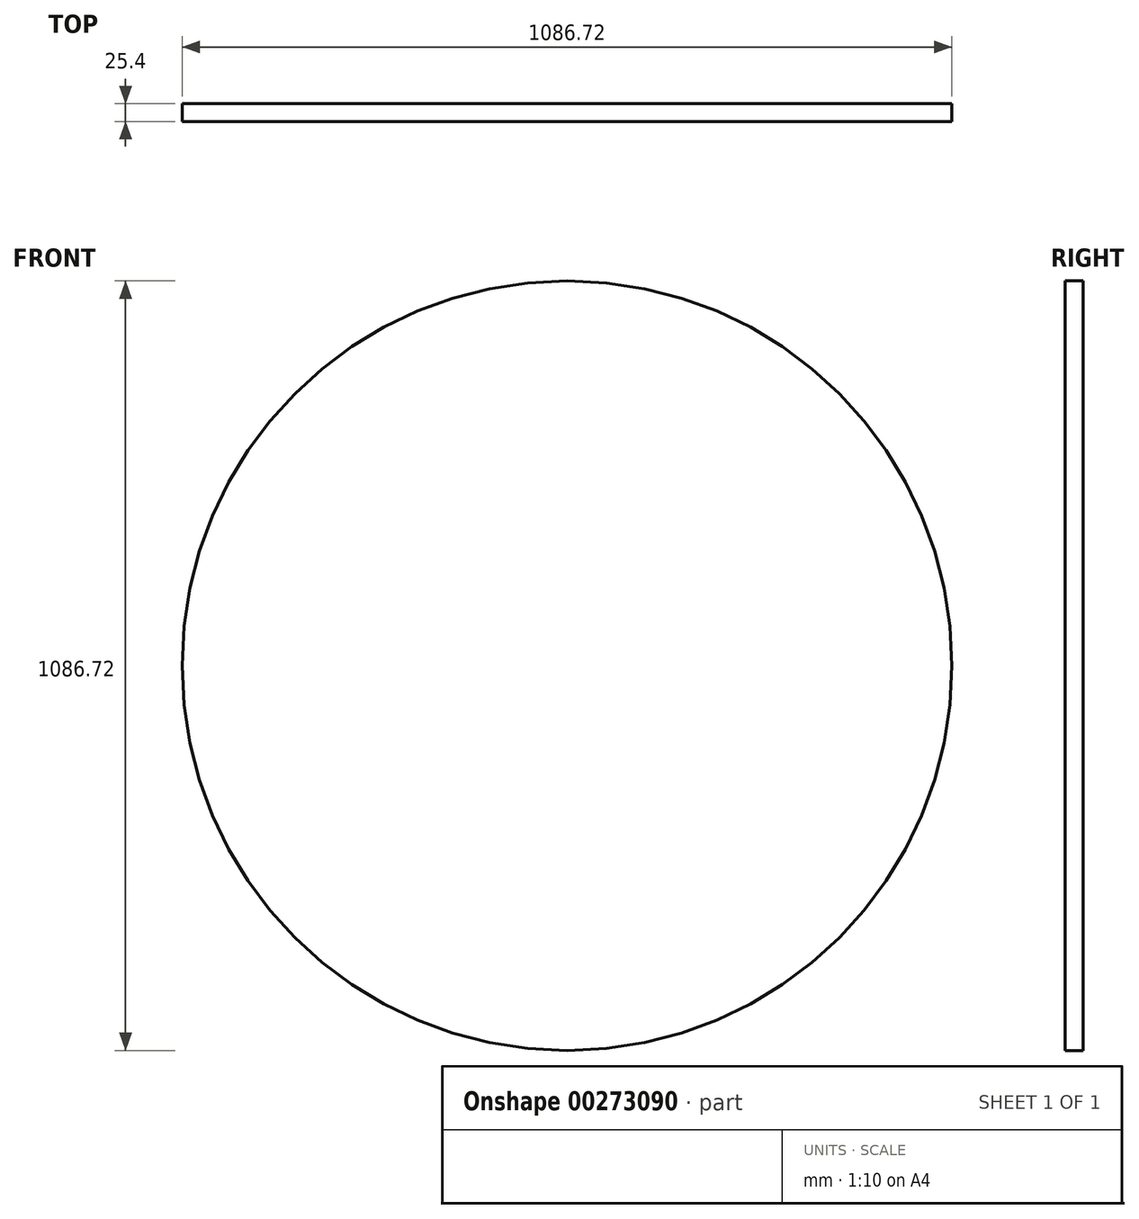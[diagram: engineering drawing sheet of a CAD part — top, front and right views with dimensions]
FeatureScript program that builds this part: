
annotation { "Feature Type Name" : "Feature", "Feature Type Description" : "" }
export const myFeature = defineFeature(function(context is Context, id is Id, definition is map)
    precondition{}
    {
        {
            var Q0;
            Q0=qCreatedBy(makeId("Front.planeOp"),FACE);
            var sketch = newSketch(context, id + "F0", { "sketchPlane" : qUnion([Q0])});
            skCircle(sketch, "E0", {"center": v(0, 0) * mm, "radius": 543.36 * mm});
            skSolve(sketch);
        }
        {
            var Q0;
            Q0=makeQuery(id+"F0.imprint","IMPRINT",FACE,{"disambiguationData":[TD([[makeQuery(id+"F0.imprint","IMPRINT",EDGE,{"derivedFrom":sQuery(id+"F0.wireOp",EDGE,"E0")}),1.0]])]});
            extrude(context, id + "F1", {"entities" : qUnion([Q0]), "depth" : 25.4 * mm});
        }
    });
